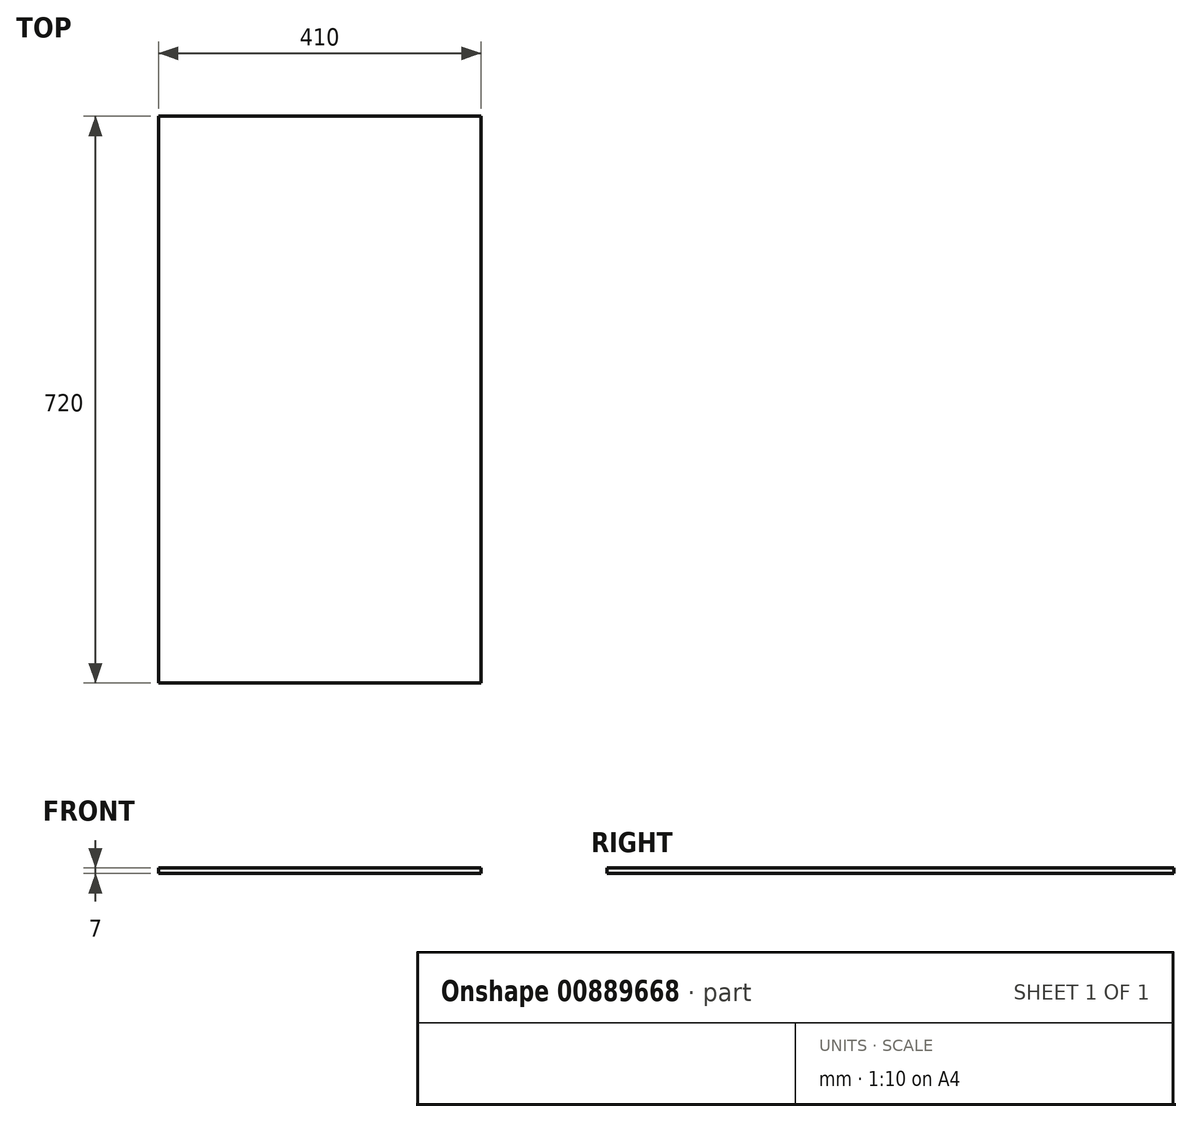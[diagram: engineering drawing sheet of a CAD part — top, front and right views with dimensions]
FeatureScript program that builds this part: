
annotation { "Feature Type Name" : "Feature", "Feature Type Description" : "" }
export const myFeature = defineFeature(function(context is Context, id is Id, definition is map)
    precondition{}
    {
        {
            var Q0;
            Q0=qCreatedBy(makeId("Top.planeOp"),FACE);
            var sketch = newSketch(context, id + "F0", { "sketchPlane" : qUnion([Q0])});
            skLineSegment(sketch, "E0.bottom", {"start": v(0, 0) * mm, "end": v(410, 0) * mm});
            skLineSegment(sketch, "E0.top", {"start": v(0, 720) * mm, "end": v(410, 720) * mm});
            skLineSegment(sketch, "E0.left", {"start": v(0, 0) * mm, "end": v(0, 720) * mm});
            skLineSegment(sketch, "E0.right", {"start": v(410, 0) * mm, "end": v(410, 720) * mm});
            skSolve(sketch);
        }
        {
            var Q0;
            Q0=makeQuery(id+"F0.imprint","IMPRINT",FACE,{"disambiguationData":[TD([[makeQuery(id+"F0.imprint","IMPRINT",EDGE,{"derivedFrom":sQuery(id+"F0.wireOp",EDGE,"E0.bottom")}),1.0]])]});
            extrude(context, id + "F1", {"entities" : qUnion([Q0]), "depth" : 7 * mm, "offsetDistance" : 25 * mm});
        }
    });
